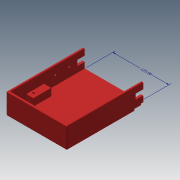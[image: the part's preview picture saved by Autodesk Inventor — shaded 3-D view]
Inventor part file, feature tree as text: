
AUTODESK INVENTOR PART (.ipt)
format: ipt  version: 2019 (Build 230136000, 136)  size: 271,872 bytes
history: native  units: mm
features: extrude x9, sketch x8, plane x3, projected_geometry x3, other x2, fillet x2
ambient origin geometry x8: Origin, YZ Plane, XZ Plane, XY Plane, X Axis, Y Axis, Z Axis, Center Point
bodies: Solid1 (feature_tree)
feature tree (27):
  other  "Annotations"
  extrude  "Extrusion1"  Depth=150.0mm
  extrude  "Extrusion2"  Depth=5.0mm
  extrude  "Extrusion3"  Depth=38.7mm TaperAngle=0.0deg
  sketch  "Sketch6"  dims[d9=3.0mm d10=20.0mm d11=0.0mm]
  fillet  "Fillet1"  Radius=3.0mm
  plane  "Work Plane4"
  extrude  "Extrusion8"  Depth=20.0mm TaperAngle=0.0deg
  extrude  "Extrusion9"  Depth=2.5mm TaperAngle=0.0deg
  fillet  "Fillet4"  Radius=35.0mm
  extrude  "Extrusion10"  Depth=16.0mm
  plane  "Work Plane5"
  extrude  "Extrusion11"  TaperAngle=0.0deg  [1 undecoded]
  plane  "Work Plane3"
  extrude  "Extrusion13"  Depth=40.0mm
  extrude  "Extrusion14"  Depth=16.0mm
  sketch  "Sketch1"  dims[d0=135.0mm d1=150.0mm]
  sketch  "Sketch3"  dims[d2=8.0mm d3=0.0mm d4=5.0mm]
  projected_geometry  "Projected Loop2"
  sketch  "Sketch4"  dims[d5=5.0mm d6=38.7mm d7=0.0mm d8=3.0mm]
  projected_geometry  "Projected Loop3"
  sketch  "Sketch15"  dims[d25=2.0mm d37=2.5mm d38=0.0mm d39=35.0mm]
  projected_geometry  "Projected Loop7"
  sketch  "Sketch16"  dims[d40=0.0mm d41=16.0mm]
  sketch  "Sketch17"  dims[d42=40.0mm d43=0.0mm]
  sketch  "Sketch21"  dims[d44=0.0mm d45=40.0mm d46=16.0mm d47=16.0mm d48=0.0mm d49=1.0mm d50=4.5mm d51=6.0mm d52=9.0mm d53=4.5mm d54=7.0mm d56=12.0mm d57=0.0mm d60=4.5mm d61=4.5mm d62=30.8mm d65=0.0mm d66=0.0mm d67=100.0mm d76=-1.5mm d78=7.5mm d79=7.5mm d80=3.15mm d81=0.0mm d90=12.5mm d91=18.0mm d92=13.0mm d93=17.0mm d94=12.0mm d95=10.0mm d96=0.0mm d73=4.870635mm d74=1.41766mm d75=125.0mm]
  other  "Linear Dimension 1"
note: 1 required parameter value undecoded (feature->parameter linkage not recoverable at this tier; creation-order binding heuristic only, values carry confidence <= 0.55)
